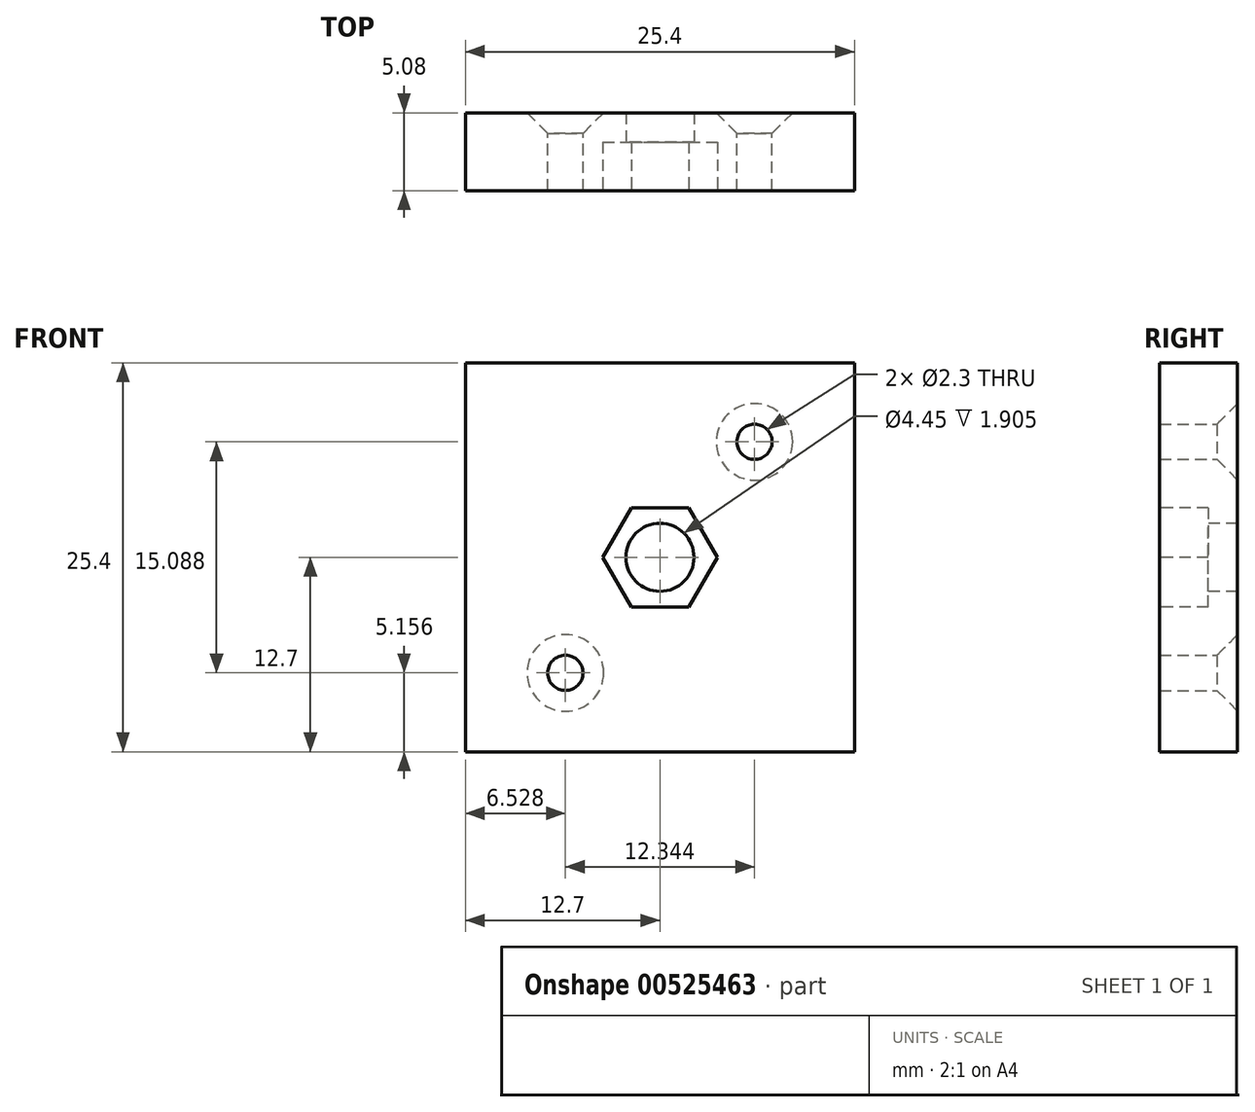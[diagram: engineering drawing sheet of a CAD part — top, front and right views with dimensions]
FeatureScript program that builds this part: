
annotation { "Feature Type Name" : "Feature", "Feature Type Description" : "" }
export const myFeature = defineFeature(function(context is Context, id is Id, definition is map)
    precondition{}
    {
        {
            var Q0;
            Q0=qCreatedBy(makeId("Front.planeOp"),FACE);
            var sketch = newSketch(context, id + "F0", { "sketchPlane" : qUnion([Q0])});
            skLineSegment(sketch, "E0.bottom", {"start": v(12.7, 12.7) * mm, "end": v(-12.7, 12.7) * mm});
            skLineSegment(sketch, "E0.top", {"start": v(12.7, -12.7) * mm, "end": v(-12.7, -12.7) * mm});
            skLineSegment(sketch, "E0.left", {"start": v(12.7, 12.7) * mm, "end": v(12.7, -12.7) * mm});
            skLineSegment(sketch, "E0.right", {"start": v(-12.7, 12.7) * mm, "end": v(-12.7, -12.7) * mm});
            skPoint(sketch, "E0.middle", {"position": v(0, 0) * mm});
            skSolve(sketch);
        }
        {
            var Q0;
            Q0 = qSketchRegion(id + "F0", true);
            extrude(context, id + "F1", {"entities" : qUnion([Q0]), "depth" : 5.08 * mm, "offsetDistance" : 25.4 * mm});
        }
        {
            var Q0;
            Q0=qCreatedBy(makeId("Front.planeOp"),FACE);
            var sketch = newSketch(context, id + "F2", { "sketchPlane" : qUnion([Q0])});
            skLineSegment(sketch, "E1.bottom", {"start": v(6.17, 7.54) * mm, "end": v(-6.17, 7.54) * mm});
            skLineSegment(sketch, "E1.top", {"start": v(6.17, -7.54) * mm, "end": v(-6.17, -7.54) * mm});
            skLineSegment(sketch, "E1.left", {"start": v(6.17, 7.54) * mm, "end": v(6.17, -7.54) * mm});
            skLineSegment(sketch, "E1.right", {"start": v(-6.17, 7.54) * mm, "end": v(-6.17, -7.54) * mm});
            skPoint(sketch, "E1.middle", {"position": v(0, 0) * mm});
            skSolve(sketch);
        }
        {
            var Q0;
            Q0=sQuery(id+"F2.wireOp",VERTEX,"E1.bottom.start");
            var Q1;
            Q1=sQuery(id+"F2.wireOp",VERTEX,"E1.top.end");
            var Q2;
            Q2=makeQuery(id+"F1.opExtrude","SWEPT_BODY",BODY,{"disambiguationData":[OSD([sQuery(id+"F0.wireOp",EDGE,"E0.bottom"),sQuery(id+"F0.wireOp",EDGE,"E0.top"),sQuery(id+"F0.wireOp",EDGE,"E0.left"),sQuery(id+"F0.wireOp",EDGE,"E0.right")])]});
            hole(context, id + "F3", {"style" : HoleStyle.C_SINK, "endStyle" : HoleEndStyle.THROUGH, "oppositeDirection" : true, "holeDiameter" : 2.3 * mm, "cSinkDiameter" : 5 * mm, "cSinkAngle" : 90 * degree, "isTappedThrough" : true, "tappedDepth" : 12.7 * mm, "tapClearance" : 3, "startFromSketch" : true, "locations" : qUnion([Q0, Q1]), "scope" : qUnion([Q2])});
        }
        {
            var Q0;
            Q0=makeQuery(id+"F1.opExtrude","CAP_FACE",FACE,{"disambiguationData":[OSD([sQuery(id+"F0.wireOp",EDGE,"E0.bottom"),sQuery(id+"F0.wireOp",EDGE,"E0.top"),sQuery(id+"F0.wireOp",EDGE,"E0.left"),sQuery(id+"F0.wireOp",EDGE,"E0.right")])],"isStart":false});
            var sketch = newSketch(context, id + "F4", { "sketchPlane" : qUnion([Q0])});
            skCircle(sketch, "E2.cCircle", {"center": v(0, 0) * mm, "radius": 3.24 * mm, "construction": true});
            skLineSegment(sketch, "E2.0", {"start": v(1.87, 3.24) * mm, "end": v(3.74, 0) * mm});
            skLineSegment(sketch, "E2.1", {"start": v(3.74, 0) * mm, "end": v(1.87, -3.24) * mm});
            skLineSegment(sketch, "E2.2", {"start": v(1.87, -3.24) * mm, "end": v(-1.87, -3.24) * mm});
            skLineSegment(sketch, "E2.3", {"start": v(-1.87, -3.24) * mm, "end": v(-3.74, 0) * mm});
            skLineSegment(sketch, "E2.4", {"start": v(-3.74, 0) * mm, "end": v(-1.87, 3.24) * mm});
            skLineSegment(sketch, "E2.5", {"start": v(-1.87, 3.24) * mm, "end": v(1.87, 3.24) * mm});
            skPoint(sketch, "E2.0.midPoint", {"position": v(2.8, 1.62) * mm});
            skSolve(sketch);
        }
        {
            var Q0;
            Q0 = qSketchRegion(id + "F4", true);
            extrude(context, id + "F5", {"entities" : qUnion([Q0]), "operationType" : NewBodyOperationType.REMOVE, "oppositeDirection" : true, "depth" : 3.17 * mm, "offsetDistance" : 25.4 * mm});
        }
        {
            var Q0;
            Q0=makeQuery(id+"F1.opExtrude","CAP_FACE",FACE,{"disambiguationData":[OSD([sQuery(id+"F0.wireOp",EDGE,"E0.bottom"),sQuery(id+"F0.wireOp",EDGE,"E0.top"),sQuery(id+"F0.wireOp",EDGE,"E0.left"),sQuery(id+"F0.wireOp",EDGE,"E0.right")])],"isStart":false});
            var sketch = newSketch(context, id + "F6", { "sketchPlane" : qUnion([Q0])});
            skCircle(sketch, "E3", {"center": v(0, 0) * mm, "radius": 2.22 * mm});
            skSolve(sketch);
        }
        {
            var Q0;
            Q0 = qSketchRegion(id + "F6", true);
            extrude(context, id + "F7", {"entities" : qUnion([Q0]), "operationType" : NewBodyOperationType.REMOVE, "endBound" : BoundingType.THROUGH_ALL, "oppositeDirection" : true, "depth" : 25.4 * mm, "offsetDistance" : 25.4 * mm});
        }
    });
